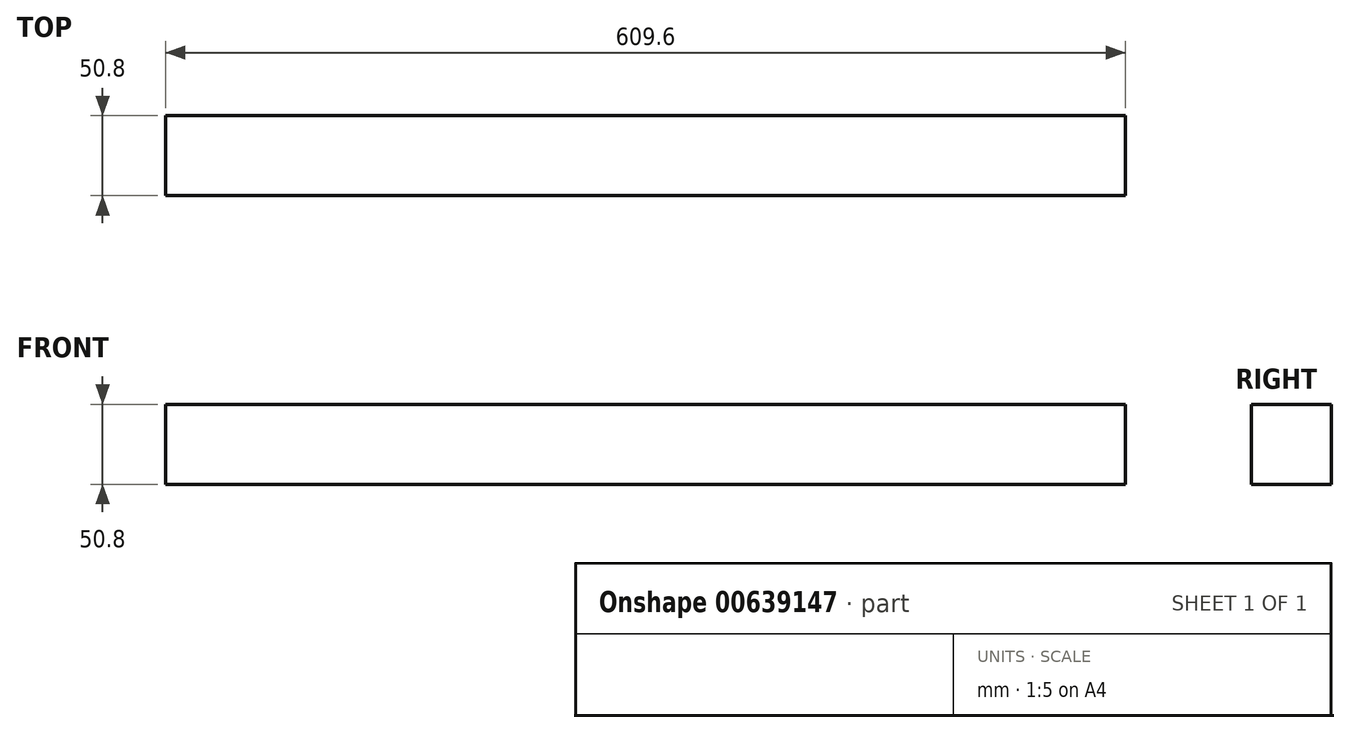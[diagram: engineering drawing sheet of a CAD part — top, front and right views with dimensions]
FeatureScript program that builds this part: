
annotation { "Feature Type Name" : "Feature", "Feature Type Description" : "" }
export const myFeature = defineFeature(function(context is Context, id is Id, definition is map)
    precondition{}
    {
        {
            var Q0;
            Q0=qCreatedBy(makeId("Right.planeOp"),FACE);
            var sketch = newSketch(context, id + "F0", { "sketchPlane" : qUnion([Q0])});
            skLineSegment(sketch, "E0.bottom", {"start": v(0, 0) * mm, "end": v(50.8, 0) * mm});
            skLineSegment(sketch, "E0.top", {"start": v(0, 50.8) * mm, "end": v(50.8, 50.8) * mm});
            skLineSegment(sketch, "E0.left", {"start": v(0, 0) * mm, "end": v(0, 50.8) * mm});
            skLineSegment(sketch, "E0.right", {"start": v(50.8, 0) * mm, "end": v(50.8, 50.8) * mm});
            skSolve(sketch);
        }
        {
            var Q0;
            Q0=makeQuery(id+"F0.imprint","IMPRINT",FACE,{"disambiguationData":[TD([[makeQuery(id+"F0.imprint","IMPRINT",EDGE,{"derivedFrom":sQuery(id+"F0.wireOp",EDGE,"E0.bottom")}),1.0]])]});
            extrude(context, id + "F1", {"entities" : qUnion([Q0]), "depth" : 609.6 * mm, "offsetDistance" : 25.4 * mm});
        }
    });
